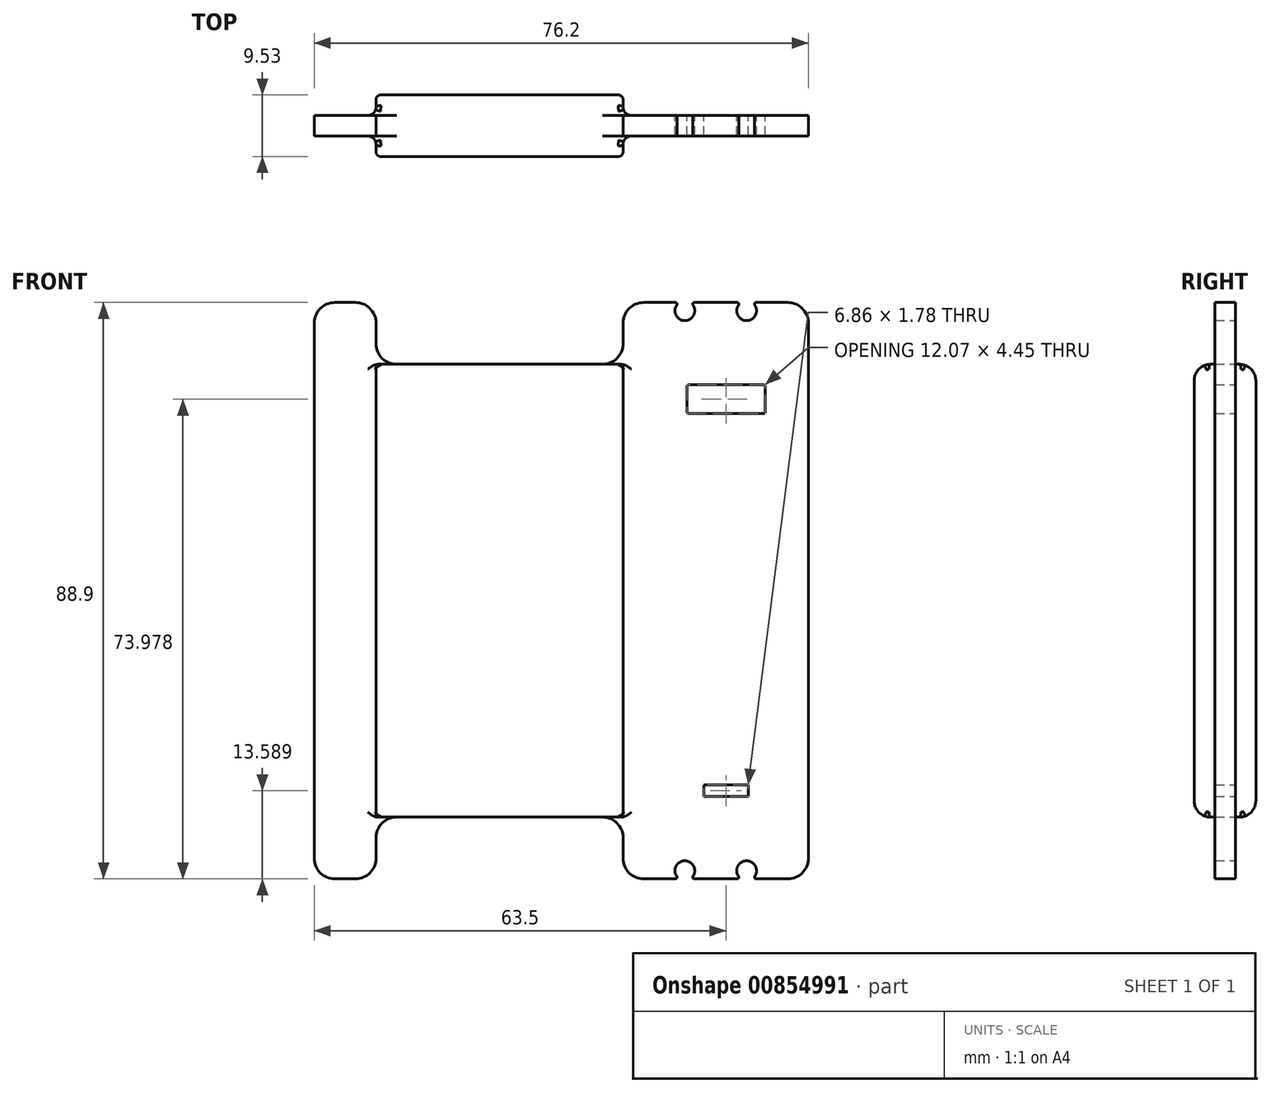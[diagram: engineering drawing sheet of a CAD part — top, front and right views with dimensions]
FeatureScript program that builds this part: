
annotation { "Feature Type Name" : "Feature", "Feature Type Description" : "" }
export const myFeature = defineFeature(function(context is Context, id is Id, definition is map)
    precondition{}
    {
        {
            var Q0;
            Q0=qCreatedBy(makeId("Front.planeOp"),FACE);
            var sketch = newSketch(context, id + "F0", { "sketchPlane" : qUnion([Q0])});
            skLineSegment(sketch, "E0.bottom", {"start": v(34.93, 44.45) * mm, "end": v(12.7, 44.45) * mm});
            skLineSegment(sketch, "E0.top", {"start": v(34.93, -44.45) * mm, "end": v(12.7, -44.45) * mm});
            skLineSegment(sketch, "E0.left", {"start": v(38.1, 41.28) * mm, "end": v(38.1, -41.28) * mm});
            skLineSegment(sketch, "E0.right", {"start": v(-38.1, 41.28) * mm, "end": v(-38.1, -41.28) * mm});
            skPoint(sketch, "E0.middle", {"position": v(0, 0) * mm});
            skLineSegment(sketch, "E1.0", {"start": v(6.35, 34.93) * mm, "end": v(-25.4, 34.93) * mm});
            skLineSegment(sketch, "E2.0", {"start": v(6.35, -34.93) * mm, "end": v(-25.4, -34.93) * mm});
            skLineSegment(sketch, "E3.0", {"start": v(-28.58, 41.28) * mm, "end": v(-28.58, 38.1) * mm});
            skLineSegment(sketch, "E4.0", {"start": v(9.53, 41.28) * mm, "end": v(9.53, 38.1) * mm});
            skLineSegment(sketch, "E5.trimOffspring", {"start": v(-31.75, 44.45) * mm, "end": v(-34.93, 44.45) * mm});
            skLineSegment(sketch, "E6.trimOffspring", {"start": v(-28.58, -38.1) * mm, "end": v(-28.58, -41.28) * mm});
            skLineSegment(sketch, "E7.trimOffspring", {"start": v(9.52, -38.1) * mm, "end": v(9.52, -41.28) * mm});
            skLineSegment(sketch, "E8.trimOffspring", {"start": v(-31.75, -44.45) * mm, "end": v(-34.93, -44.45) * mm});
            skPoint(sketch, "E9.visualSharp", {"position": v(-38.1, 44.45) * mm});
            skArc(sketch, "E9.filletArc", {"start": v(-34.93, 44.45) * mm, "mid": v(-37.17, 43.52) * mm, "end": v(-38.1, 41.28) * mm});
            skPoint(sketch, "E10.visualSharp", {"position": v(-28.58, 44.45) * mm});
            skArc(sketch, "E10.filletArc", {"start": v(-28.57, 41.28) * mm, "mid": v(-29.5, 43.52) * mm, "end": v(-31.75, 44.45) * mm});
            skPoint(sketch, "E11.visualSharp", {"position": v(-28.58, 34.93) * mm});
            skArc(sketch, "E11.filletArc", {"start": v(-28.58, 38.1) * mm, "mid": v(-27.65, 35.85) * mm, "end": v(-25.4, 34.92) * mm});
            skPoint(sketch, "E12.visualSharp", {"position": v(9.53, 34.93) * mm});
            skArc(sketch, "E12.filletArc", {"start": v(6.35, 34.93) * mm, "mid": v(8.6, 35.85) * mm, "end": v(9.53, 38.1) * mm});
            skPoint(sketch, "E13.visualSharp", {"position": v(9.53, 44.45) * mm});
            skArc(sketch, "E13.filletArc", {"start": v(12.7, 44.45) * mm, "mid": v(10.45, 43.52) * mm, "end": v(9.52, 41.28) * mm});
            skPoint(sketch, "E14.visualSharp", {"position": v(38.1, 44.45) * mm});
            skArc(sketch, "E14.filletArc", {"start": v(38.1, 41.28) * mm, "mid": v(37.17, 43.52) * mm, "end": v(34.93, 44.45) * mm});
            skPoint(sketch, "E15.visualSharp", {"position": v(38.1, -44.45) * mm});
            skArc(sketch, "E15.filletArc", {"start": v(34.93, -44.45) * mm, "mid": v(37.17, -43.52) * mm, "end": v(38.1, -41.28) * mm});
            skPoint(sketch, "E16.visualSharp", {"position": v(9.52, -44.45) * mm});
            skArc(sketch, "E16.filletArc", {"start": v(9.52, -41.28) * mm, "mid": v(10.45, -43.52) * mm, "end": v(12.7, -44.45) * mm});
            skPoint(sketch, "E17.visualSharp", {"position": v(9.52, -34.92) * mm});
            skArc(sketch, "E17.filletArc", {"start": v(9.52, -38.1) * mm, "mid": v(8.6, -35.85) * mm, "end": v(6.35, -34.93) * mm});
            skPoint(sketch, "E18.visualSharp", {"position": v(-28.58, -34.93) * mm});
            skArc(sketch, "E18.filletArc", {"start": v(-25.4, -34.93) * mm, "mid": v(-27.65, -35.85) * mm, "end": v(-28.58, -38.1) * mm});
            skPoint(sketch, "E19.visualSharp", {"position": v(-28.58, -44.45) * mm});
            skArc(sketch, "E19.filletArc", {"start": v(-31.75, -44.45) * mm, "mid": v(-29.5, -43.52) * mm, "end": v(-28.58, -41.28) * mm});
            skPoint(sketch, "E20.visualSharp", {"position": v(-38.1, -44.45) * mm});
            skArc(sketch, "E20.filletArc", {"start": v(-38.1, -41.28) * mm, "mid": v(-37.17, -43.52) * mm, "end": v(-34.93, -44.45) * mm});
            skSolve(sketch);
        }
        {
            var Q0;
            Q0=makeQuery(id+"F0.imprint","IMPRINT",FACE,{"disambiguationData":[TD([[makeQuery(id+"F0.imprint","IMPRINT",EDGE,{"derivedFrom":sQuery(id+"F0.wireOp",EDGE,"E0.bottom")}),1.0]])]});
            extrude(context, id + "F1", {"entities" : qUnion([Q0]), "depth" : 3.17 * mm, "offsetDistance" : 25.4 * mm});
        }
        {
            var Q0;
            Q0=qCreatedBy(makeId("Front.planeOp"),FACE);
            var sketch = newSketch(context, id + "F2", { "sketchPlane" : qUnion([Q0])});
            skLineSegment(sketch, "E21.bottom", {"start": v(19.37, 31.75) * mm, "end": v(31.43, 31.75) * mm});
            skLineSegment(sketch, "E21.top", {"start": v(19.37, 27.3) * mm, "end": v(31.43, 27.3) * mm});
            skLineSegment(sketch, "E21.left", {"start": v(19.37, 31.75) * mm, "end": v(19.37, 27.3) * mm});
            skLineSegment(sketch, "E21.right", {"start": v(31.43, 31.75) * mm, "end": v(31.43, 27.3) * mm});
            skLineSegment(sketch, "E22.bottom", {"start": v(21.97, -29.97) * mm, "end": v(28.83, -29.97) * mm});
            skLineSegment(sketch, "E22.top", {"start": v(21.97, -31.75) * mm, "end": v(28.83, -31.75) * mm});
            skLineSegment(sketch, "E22.left", {"start": v(21.97, -29.97) * mm, "end": v(21.97, -31.75) * mm});
            skLineSegment(sketch, "E22.right", {"start": v(28.83, -29.97) * mm, "end": v(28.83, -31.75) * mm});
            skPoint(sketch, "E23", {"position": v(25.4, 31.75) * mm});
            skPoint(sketch, "E24", {"position": v(25.4, -29.97) * mm});
            skCircle(sketch, "E25", {"center": v(28.58, 43.18) * mm, "radius": 1.52 * mm});
            skCircle(sketch, "E26", {"center": v(28.58, -43.18) * mm, "radius": 1.52 * mm});
            skCircle(sketch, "E27", {"center": v(19.05, -43.18) * mm, "radius": 1.52 * mm});
            skCircle(sketch, "E28", {"center": v(19.05, 43.18) * mm, "radius": 1.52 * mm});
            skSolve(sketch);
        }
        {
            var Q0;
            Q0=makeQuery(id+"F2.imprint","IMPRINT",FACE,{"disambiguationData":[TD([[makeQuery(id+"F2.imprint","IMPRINT",EDGE,{"derivedFrom":sQuery(id+"F2.wireOp",EDGE,"E21.bottom")}),-1.0]])]});
            var Q1;
            Q1=makeQuery(id+"F2.imprint","IMPRINT",FACE,{"disambiguationData":[TD([[makeQuery(id+"F2.imprint","IMPRINT",EDGE,{"derivedFrom":sQuery(id+"F2.wireOp",EDGE,"E22.bottom")}),-1.0]])]});
            var Q2;
            Q2=makeQuery(id+"F2.imprint","IMPRINT",FACE,{"disambiguationData":[TD([[makeQuery(id+"F2.imprint","IMPRINT",EDGE,{"derivedFrom":sQuery(id+"F2.wireOp",EDGE,"E25")}),1.0]])]});
            var Q3;
            Q3=makeQuery(id+"F2.imprint","IMPRINT",FACE,{"disambiguationData":[TD([[makeQuery(id+"F2.imprint","IMPRINT",EDGE,{"derivedFrom":sQuery(id+"F2.wireOp",EDGE,"E28")}),1.0]])]});
            var Q4;
            Q4=makeQuery(id+"F2.imprint","IMPRINT",FACE,{"disambiguationData":[TD([[makeQuery(id+"F2.imprint","IMPRINT",EDGE,{"derivedFrom":sQuery(id+"F2.wireOp",EDGE,"E27")}),1.0]])]});
            var Q5;
            Q5=makeQuery(id+"F2.imprint","IMPRINT",FACE,{"disambiguationData":[TD([[makeQuery(id+"F2.imprint","IMPRINT",EDGE,{"derivedFrom":sQuery(id+"F2.wireOp",EDGE,"E26")}),1.0]])]});
            extrude(context, id + "F3", {"entities" : qUnion([Q0, Q1, Q2, Q3, Q4, Q5]), "operationType" : NewBodyOperationType.REMOVE, "endBound" : BoundingType.THROUGH_ALL, "depth" : 25.4 * mm, "offsetDistance" : 25.4 * mm});
        }
        {
            var Q0;
            Q0=makeQuery(id+"F3.boolean.opBoolean","INTERSECT",EDGE,{"disambiguationData":[OD(0.0)],"derivedFrom":[makeQuery(id+"F1.opExtrude","SWEPT_FACE",FACE,{"disambiguationData":[OSD([sQuery(id+"F0.wireOp",EDGE,"E0.bottom")])]}),makeQuery(id+"F3.opExtrude","SWEPT_FACE",FACE,{"disambiguationData":[OSD([sQuery(id+"F2.wireOp",EDGE,"E28")])]})]});
            var Q1;
            Q1=makeQuery(id+"F3.boolean.opBoolean","INTERSECT",EDGE,{"disambiguationData":[OD(1.0)],"derivedFrom":[makeQuery(id+"F1.opExtrude","SWEPT_FACE",FACE,{"disambiguationData":[OSD([sQuery(id+"F0.wireOp",EDGE,"E0.bottom")])]}),makeQuery(id+"F3.opExtrude","SWEPT_FACE",FACE,{"disambiguationData":[OSD([sQuery(id+"F2.wireOp",EDGE,"E28")])]})]});
            var Q2;
            Q2=makeQuery(id+"F3.boolean.opBoolean","INTERSECT",EDGE,{"disambiguationData":[OD(1.0)],"derivedFrom":[makeQuery(id+"F1.opExtrude","SWEPT_FACE",FACE,{"disambiguationData":[OSD([sQuery(id+"F0.wireOp",EDGE,"E0.bottom")])]}),makeQuery(id+"F3.opExtrude","SWEPT_FACE",FACE,{"disambiguationData":[OSD([sQuery(id+"F2.wireOp",EDGE,"E25")])]})]});
            var Q3;
            Q3=makeQuery(id+"F3.boolean.opBoolean","INTERSECT",EDGE,{"disambiguationData":[OD(0.0)],"derivedFrom":[makeQuery(id+"F1.opExtrude","SWEPT_FACE",FACE,{"disambiguationData":[OSD([sQuery(id+"F0.wireOp",EDGE,"E0.bottom")])]}),makeQuery(id+"F3.opExtrude","SWEPT_FACE",FACE,{"disambiguationData":[OSD([sQuery(id+"F2.wireOp",EDGE,"E25")])]})]});
            var Q4;
            Q4=makeQuery(id+"F3.boolean.opBoolean","INTERSECT",EDGE,{"disambiguationData":[OD(0.0)],"derivedFrom":[makeQuery(id+"F1.opExtrude","SWEPT_FACE",FACE,{"disambiguationData":[OSD([sQuery(id+"F0.wireOp",EDGE,"E0.top")])]}),makeQuery(id+"F3.opExtrude","SWEPT_FACE",FACE,{"disambiguationData":[OSD([sQuery(id+"F2.wireOp",EDGE,"E27")])]})]});
            var Q5;
            Q5=makeQuery(id+"F3.boolean.opBoolean","INTERSECT",EDGE,{"disambiguationData":[OD(1.0)],"derivedFrom":[makeQuery(id+"F1.opExtrude","SWEPT_FACE",FACE,{"disambiguationData":[OSD([sQuery(id+"F0.wireOp",EDGE,"E0.top")])]}),makeQuery(id+"F3.opExtrude","SWEPT_FACE",FACE,{"disambiguationData":[OSD([sQuery(id+"F2.wireOp",EDGE,"E27")])]})]});
            var Q6;
            Q6=makeQuery(id+"F3.boolean.opBoolean","INTERSECT",EDGE,{"disambiguationData":[OD(1.0)],"derivedFrom":[makeQuery(id+"F1.opExtrude","SWEPT_FACE",FACE,{"disambiguationData":[OSD([sQuery(id+"F0.wireOp",EDGE,"E0.top")])]}),makeQuery(id+"F3.opExtrude","SWEPT_FACE",FACE,{"disambiguationData":[OSD([sQuery(id+"F2.wireOp",EDGE,"E26")])]})]});
            var Q7;
            Q7=makeQuery(id+"F3.boolean.opBoolean","INTERSECT",EDGE,{"disambiguationData":[OD(0.0)],"derivedFrom":[makeQuery(id+"F1.opExtrude","SWEPT_FACE",FACE,{"disambiguationData":[OSD([sQuery(id+"F0.wireOp",EDGE,"E0.top")])]}),makeQuery(id+"F3.opExtrude","SWEPT_FACE",FACE,{"disambiguationData":[OSD([sQuery(id+"F2.wireOp",EDGE,"E26")])]})]});
            var Q8;
            Q8=makeQuery(id+"F3.boolean.opBoolean","COPY",EDGE,{"derivedFrom":makeQuery(id+"F3.opExtrude","SWEPT_EDGE",EDGE,{"disambiguationData":[OSD([sQuery(id+"F2.wireOp",EDGE,"E21.bottom"),sQuery(id+"F2.wireOp",EDGE,"E21.left")])]})});
            var Q9;
            Q9=makeQuery(id+"F3.boolean.opBoolean","COPY",EDGE,{"derivedFrom":makeQuery(id+"F3.opExtrude","SWEPT_EDGE",EDGE,{"disambiguationData":[OSD([sQuery(id+"F2.wireOp",EDGE,"E21.top"),sQuery(id+"F2.wireOp",EDGE,"E21.left")])]})});
            var Q10;
            Q10=makeQuery(id+"F3.boolean.opBoolean","COPY",EDGE,{"derivedFrom":makeQuery(id+"F3.opExtrude","SWEPT_EDGE",EDGE,{"disambiguationData":[OSD([sQuery(id+"F2.wireOp",EDGE,"E21.top"),sQuery(id+"F2.wireOp",EDGE,"E21.right")])]})});
            var Q11;
            Q11=makeQuery(id+"F3.boolean.opBoolean","COPY",EDGE,{"derivedFrom":makeQuery(id+"F3.opExtrude","SWEPT_EDGE",EDGE,{"disambiguationData":[OSD([sQuery(id+"F2.wireOp",EDGE,"E21.bottom"),sQuery(id+"F2.wireOp",EDGE,"E21.right")])]})});
            fillet(context, id + "F4", {"entities" : qUnion([Q0, Q1, Q2, Q3, Q4, Q5, Q6, Q7, Q8, Q9, Q10, Q11]), "radius" : 0.25 * mm, "tangentPropagation" : true, "allowEdgeOverflow" : false});
        }
        {
            var Q0;
            Q0=qCreatedBy(makeId("Right.planeOp"),FACE);
            var sketch = newSketch(context, id + "F5", { "sketchPlane" : qUnion([Q0])});
            skLineSegment(sketch, "E29.0.1", {"start": v(0, 34.92) * mm, "end": v(-3.18, 34.92) * mm});
            skLineSegment(sketch, "E29.0.3", {"start": v(-3.81, 34.93) * mm, "end": v(0.63, 34.93) * mm});
            skLineSegment(sketch, "E30.0.1", {"start": v(0, -34.93) * mm, "end": v(-3.18, -34.93) * mm});
            skLineSegment(sketch, "E30.0.3", {"start": v(-3.81, -34.93) * mm, "end": v(0.63, -34.93) * mm});
            skLineSegment(sketch, "E31", {"start": v(-6.35, 32.39) * mm, "end": v(-6.35, -32.38) * mm});
            skLineSegment(sketch, "E32", {"start": v(-1.59, 34.93) * mm, "end": v(-1.59, -34.93) * mm, "construction": true});
            skLineSegment(sketch, "E33.MirrorCS", {"start": v(3.17, 32.39) * mm, "end": v(3.17, -32.39) * mm});
            skPoint(sketch, "E34.orphan", {"position": v(-3.18, 34.93) * mm});
            skPoint(sketch, "E35.orphan", {"position": v(0, 34.93) * mm});
            skPoint(sketch, "E36.orphan", {"position": v(-3.18, -34.93) * mm});
            skPoint(sketch, "E37.orphan", {"position": v(0, -34.93) * mm});
            skPoint(sketch, "E38.visualSharp", {"position": v(-6.35, 34.93) * mm});
            skArc(sketch, "E38.filletArc", {"start": v(-3.81, 34.93) * mm, "mid": v(-5.6, 34.18) * mm, "end": v(-6.35, 32.39) * mm});
            skPoint(sketch, "E39.visualSharp", {"position": v(3.17, 34.93) * mm});
            skArc(sketch, "E39.filletArc", {"start": v(3.17, 32.39) * mm, "mid": v(2.43, 34.18) * mm, "end": v(0.63, 34.93) * mm});
            skPoint(sketch, "E40.visualSharp", {"position": v(3.17, -34.93) * mm});
            skArc(sketch, "E40.filletArc", {"start": v(0.63, -34.93) * mm, "mid": v(2.43, -34.18) * mm, "end": v(3.17, -32.39) * mm});
            skPoint(sketch, "E41.visualSharp", {"position": v(-6.35, -34.93) * mm});
            skArc(sketch, "E41.filletArc", {"start": v(-6.35, -32.39) * mm, "mid": v(-5.6, -34.18) * mm, "end": v(-3.81, -34.93) * mm});
            skSolve(sketch);
        }
        {
            var Q0;
            Q0 = qSketchRegion(id + "F5", true);
            var Q1;
            Q1=makeQuery(id+"F1.opExtrude","CAP_VERTEX",VERTEX,{"disambiguationData":[OSD([sQuery(id+"F0.wireOp",EDGE,"E4.0"),sQuery(id+"F0.wireOp",EDGE,"E12.filletArc")])],"isStart":false});
            var Q2;
            Q2=makeQuery(id+"F1.opExtrude","CAP_VERTEX",VERTEX,{"disambiguationData":[OSD([sQuery(id+"F0.wireOp",EDGE,"E3.0"),sQuery(id+"F0.wireOp",EDGE,"E11.filletArc")])],"isStart":false});
            extrude(context, id + "F6", {"entities" : qUnion([Q0]), "operationType" : NewBodyOperationType.ADD, "endBound" : BoundingType.UP_TO_VERTEX, "depth" : 25.4 * mm, "endBoundEntityVertex" : qUnion([Q1]), "offsetDistance" : 25.4 * mm, "hasSecondDirection" : true, "secondDirectionBound" : SecondDirectionBoundingType.UP_TO_VERTEX, "secondDirectionOppositeDirection" : true, "secondDirectionDepth" : 25.4 * mm, "secondDirectionBoundEntityVertex" : qUnion([Q2])});
        }
        {
            var Q0;
            Q0=makeQuery(id+"F6.boolean.opBoolean","INTERSECT",EDGE,{"derivedFrom":[makeQuery(id+"F1.opExtrude","CAP_FACE",FACE,{"disambiguationData":[OSD([sQuery(id+"F0.wireOp",EDGE,"E0.bottom"),sQuery(id+"F0.wireOp",EDGE,"E0.top"),sQuery(id+"F0.wireOp",EDGE,"E0.left"),sQuery(id+"F0.wireOp",EDGE,"E0.right"),sQuery(id+"F0.wireOp",EDGE,"E1.0"),sQuery(id+"F0.wireOp",EDGE,"E2.0"),sQuery(id+"F0.wireOp",EDGE,"E3.0"),sQuery(id+"F0.wireOp",EDGE,"E4.0"),sQuery(id+"F0.wireOp",EDGE,"E5.trimOffspring"),sQuery(id+"F0.wireOp",EDGE,"E6.trimOffspring"),sQuery(id+"F0.wireOp",EDGE,"E7.trimOffspring"),sQuery(id+"F0.wireOp",EDGE,"E8.trimOffspring"),sQuery(id+"F0.wireOp",EDGE,"E9.filletArc"),sQuery(id+"F0.wireOp",EDGE,"E10.filletArc"),sQuery(id+"F0.wireOp",EDGE,"E11.filletArc"),sQuery(id+"F0.wireOp",EDGE,"E12.filletArc"),sQuery(id+"F0.wireOp",EDGE,"E13.filletArc"),sQuery(id+"F0.wireOp",EDGE,"E14.filletArc"),sQuery(id+"F0.wireOp",EDGE,"E15.filletArc"),sQuery(id+"F0.wireOp",EDGE,"E16.filletArc"),sQuery(id+"F0.wireOp",EDGE,"E17.filletArc"),sQuery(id+"F0.wireOp",EDGE,"E18.filletArc"),sQuery(id+"F0.wireOp",EDGE,"E19.filletArc"),sQuery(id+"F0.wireOp",EDGE,"E20.filletArc")])],"isStart":false}),makeQuery(id+"F6.opExtrude","CAP_FACE",FACE,{"disambiguationData":[OSD([sQuery(id+"F5.wireOp",EDGE,"E29.0.1"),sQuery(id+"F5.wireOp",EDGE,"E29.0.3"),sQuery(id+"F5.wireOp",EDGE,"E30.0.1"),sQuery(id+"F5.wireOp",EDGE,"E30.0.3"),sQuery(id+"F5.wireOp",EDGE,"E31"),sQuery(id+"F5.wireOp",EDGE,"E33.MirrorCS"),sQuery(id+"F5.wireOp",EDGE,"E38.filletArc"),sQuery(id+"F5.wireOp",EDGE,"E39.filletArc"),sQuery(id+"F5.wireOp",EDGE,"E40.filletArc"),sQuery(id+"F5.wireOp",EDGE,"E41.filletArc")])],"isStart":true})]});
            var Q1;
            Q1=makeQuery(id+"F6.boolean.opBoolean","INTERSECT",EDGE,{"derivedFrom":[makeQuery(id+"F1.opExtrude","CAP_FACE",FACE,{"disambiguationData":[OSD([sQuery(id+"F0.wireOp",EDGE,"E0.bottom"),sQuery(id+"F0.wireOp",EDGE,"E0.top"),sQuery(id+"F0.wireOp",EDGE,"E0.left"),sQuery(id+"F0.wireOp",EDGE,"E0.right"),sQuery(id+"F0.wireOp",EDGE,"E1.0"),sQuery(id+"F0.wireOp",EDGE,"E2.0"),sQuery(id+"F0.wireOp",EDGE,"E3.0"),sQuery(id+"F0.wireOp",EDGE,"E4.0"),sQuery(id+"F0.wireOp",EDGE,"E5.trimOffspring"),sQuery(id+"F0.wireOp",EDGE,"E6.trimOffspring"),sQuery(id+"F0.wireOp",EDGE,"E7.trimOffspring"),sQuery(id+"F0.wireOp",EDGE,"E8.trimOffspring"),sQuery(id+"F0.wireOp",EDGE,"E9.filletArc"),sQuery(id+"F0.wireOp",EDGE,"E10.filletArc"),sQuery(id+"F0.wireOp",EDGE,"E11.filletArc"),sQuery(id+"F0.wireOp",EDGE,"E12.filletArc"),sQuery(id+"F0.wireOp",EDGE,"E13.filletArc"),sQuery(id+"F0.wireOp",EDGE,"E14.filletArc"),sQuery(id+"F0.wireOp",EDGE,"E15.filletArc"),sQuery(id+"F0.wireOp",EDGE,"E16.filletArc"),sQuery(id+"F0.wireOp",EDGE,"E17.filletArc"),sQuery(id+"F0.wireOp",EDGE,"E18.filletArc"),sQuery(id+"F0.wireOp",EDGE,"E19.filletArc"),sQuery(id+"F0.wireOp",EDGE,"E20.filletArc")])],"isStart":false}),makeQuery(id+"F6.opExtrude","CAP_FACE",FACE,{"disambiguationData":[OSD([sQuery(id+"F5.wireOp",EDGE,"E29.0.1"),sQuery(id+"F5.wireOp",EDGE,"E29.0.3"),sQuery(id+"F5.wireOp",EDGE,"E30.0.1"),sQuery(id+"F5.wireOp",EDGE,"E30.0.3"),sQuery(id+"F5.wireOp",EDGE,"E31"),sQuery(id+"F5.wireOp",EDGE,"E33.MirrorCS"),sQuery(id+"F5.wireOp",EDGE,"E38.filletArc"),sQuery(id+"F5.wireOp",EDGE,"E39.filletArc"),sQuery(id+"F5.wireOp",EDGE,"E40.filletArc"),sQuery(id+"F5.wireOp",EDGE,"E41.filletArc")])],"isStart":false})]});
            var Q2;
            Q2=makeQuery(id+"F6.boolean.opBoolean","INTERSECT",EDGE,{"derivedFrom":[makeQuery(id+"F1.opExtrude","CAP_FACE",FACE,{"disambiguationData":[OSD([sQuery(id+"F0.wireOp",EDGE,"E0.bottom"),sQuery(id+"F0.wireOp",EDGE,"E0.top"),sQuery(id+"F0.wireOp",EDGE,"E0.left"),sQuery(id+"F0.wireOp",EDGE,"E0.right"),sQuery(id+"F0.wireOp",EDGE,"E1.0"),sQuery(id+"F0.wireOp",EDGE,"E2.0"),sQuery(id+"F0.wireOp",EDGE,"E3.0"),sQuery(id+"F0.wireOp",EDGE,"E4.0"),sQuery(id+"F0.wireOp",EDGE,"E5.trimOffspring"),sQuery(id+"F0.wireOp",EDGE,"E6.trimOffspring"),sQuery(id+"F0.wireOp",EDGE,"E7.trimOffspring"),sQuery(id+"F0.wireOp",EDGE,"E8.trimOffspring"),sQuery(id+"F0.wireOp",EDGE,"E9.filletArc"),sQuery(id+"F0.wireOp",EDGE,"E10.filletArc"),sQuery(id+"F0.wireOp",EDGE,"E11.filletArc"),sQuery(id+"F0.wireOp",EDGE,"E12.filletArc"),sQuery(id+"F0.wireOp",EDGE,"E13.filletArc"),sQuery(id+"F0.wireOp",EDGE,"E14.filletArc"),sQuery(id+"F0.wireOp",EDGE,"E15.filletArc"),sQuery(id+"F0.wireOp",EDGE,"E16.filletArc"),sQuery(id+"F0.wireOp",EDGE,"E17.filletArc"),sQuery(id+"F0.wireOp",EDGE,"E18.filletArc"),sQuery(id+"F0.wireOp",EDGE,"E19.filletArc"),sQuery(id+"F0.wireOp",EDGE,"E20.filletArc")])],"isStart":true}),makeQuery(id+"F6.opExtrude","CAP_FACE",FACE,{"disambiguationData":[OSD([sQuery(id+"F5.wireOp",EDGE,"E29.0.1"),sQuery(id+"F5.wireOp",EDGE,"E29.0.3"),sQuery(id+"F5.wireOp",EDGE,"E30.0.1"),sQuery(id+"F5.wireOp",EDGE,"E30.0.3"),sQuery(id+"F5.wireOp",EDGE,"E31"),sQuery(id+"F5.wireOp",EDGE,"E33.MirrorCS"),sQuery(id+"F5.wireOp",EDGE,"E38.filletArc"),sQuery(id+"F5.wireOp",EDGE,"E39.filletArc"),sQuery(id+"F5.wireOp",EDGE,"E40.filletArc"),sQuery(id+"F5.wireOp",EDGE,"E41.filletArc")])],"isStart":true})]});
            var Q3;
            Q3=makeQuery(id+"F6.boolean.opBoolean","INTERSECT",EDGE,{"derivedFrom":[makeQuery(id+"F1.opExtrude","CAP_FACE",FACE,{"disambiguationData":[OSD([sQuery(id+"F0.wireOp",EDGE,"E0.bottom"),sQuery(id+"F0.wireOp",EDGE,"E0.top"),sQuery(id+"F0.wireOp",EDGE,"E0.left"),sQuery(id+"F0.wireOp",EDGE,"E0.right"),sQuery(id+"F0.wireOp",EDGE,"E1.0"),sQuery(id+"F0.wireOp",EDGE,"E2.0"),sQuery(id+"F0.wireOp",EDGE,"E3.0"),sQuery(id+"F0.wireOp",EDGE,"E4.0"),sQuery(id+"F0.wireOp",EDGE,"E5.trimOffspring"),sQuery(id+"F0.wireOp",EDGE,"E6.trimOffspring"),sQuery(id+"F0.wireOp",EDGE,"E7.trimOffspring"),sQuery(id+"F0.wireOp",EDGE,"E8.trimOffspring"),sQuery(id+"F0.wireOp",EDGE,"E9.filletArc"),sQuery(id+"F0.wireOp",EDGE,"E10.filletArc"),sQuery(id+"F0.wireOp",EDGE,"E11.filletArc"),sQuery(id+"F0.wireOp",EDGE,"E12.filletArc"),sQuery(id+"F0.wireOp",EDGE,"E13.filletArc"),sQuery(id+"F0.wireOp",EDGE,"E14.filletArc"),sQuery(id+"F0.wireOp",EDGE,"E15.filletArc"),sQuery(id+"F0.wireOp",EDGE,"E16.filletArc"),sQuery(id+"F0.wireOp",EDGE,"E17.filletArc"),sQuery(id+"F0.wireOp",EDGE,"E18.filletArc"),sQuery(id+"F0.wireOp",EDGE,"E19.filletArc"),sQuery(id+"F0.wireOp",EDGE,"E20.filletArc")])],"isStart":true}),makeQuery(id+"F6.opExtrude","CAP_FACE",FACE,{"disambiguationData":[OSD([sQuery(id+"F5.wireOp",EDGE,"E29.0.1"),sQuery(id+"F5.wireOp",EDGE,"E29.0.3"),sQuery(id+"F5.wireOp",EDGE,"E30.0.1"),sQuery(id+"F5.wireOp",EDGE,"E30.0.3"),sQuery(id+"F5.wireOp",EDGE,"E31"),sQuery(id+"F5.wireOp",EDGE,"E33.MirrorCS"),sQuery(id+"F5.wireOp",EDGE,"E38.filletArc"),sQuery(id+"F5.wireOp",EDGE,"E39.filletArc"),sQuery(id+"F5.wireOp",EDGE,"E40.filletArc"),sQuery(id+"F5.wireOp",EDGE,"E41.filletArc")])],"isStart":false})]});
            fillet(context, id + "F7", {"entities" : qUnion([Q0, Q1, Q2, Q3]), "tangentPropagation" : true, "radius" : 1.27 * mm, "defaultsChanged" : false, "vertexSettings" : [], "allowEdgeOverflow" : false});
        }
        {
            var Q0;
            Q0=makeQuery(id+"F6.opExtrude","CAP_EDGE",EDGE,{"disambiguationData":[OSD([sQuery(id+"F5.wireOp",EDGE,"E31")])],"isStart":false});
            var Q1;
            Q1=makeQuery(id+"F6.opExtrude","CAP_EDGE",EDGE,{"disambiguationData":[OSD([sQuery(id+"F5.wireOp",EDGE,"E31")])],"isStart":true});
            var Q2;
            Q2=makeQuery(id+"F6.opExtrude","CAP_EDGE",EDGE,{"disambiguationData":[OSD([sQuery(id+"F5.wireOp",EDGE,"E33.MirrorCS")])],"isStart":false});
            var Q3;
            Q3=makeQuery(id+"F6.opExtrude","CAP_EDGE",EDGE,{"disambiguationData":[OSD([sQuery(id+"F5.wireOp",EDGE,"E33.MirrorCS")])],"isStart":true});
            fillet(context, id + "F8", {"entities" : qUnion([Q0, Q1, Q2, Q3]), "tangentPropagation" : true, "radius" : 0.76 * mm, "defaultsChanged" : false, "vertexSettings" : [], "allowEdgeOverflow" : false});
        }
    });
